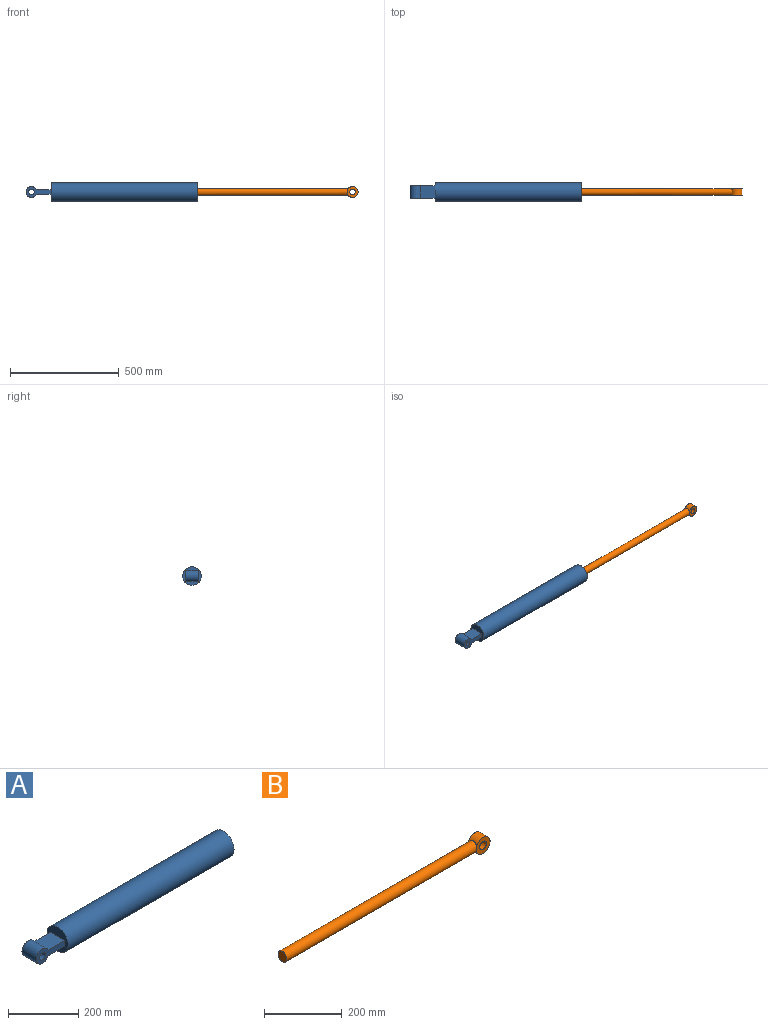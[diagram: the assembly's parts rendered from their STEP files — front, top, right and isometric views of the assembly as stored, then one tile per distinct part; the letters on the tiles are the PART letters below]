
ASSEMBLY  parts=2 mates=1
PART A: 11 faces, bbox 785x85x85 mm
  f0: cylinder r=42.5mm len=670mm, axis (-1,0,0), area 178913.7mm2, adj f1,f2
  f1: plane 85x85mm, normal (1,0,0), area 4870.3mm2, adj f0,f9
  f2: plane 85x85mm, normal (-1,0,0), area 4514.5mm2, adj f0,f3,f4,f5,f6
  f3: plane 67.09x58mm, normal (0,0,1), area 3891.1mm2, adj f2,f4,f6,f7
  f4: plane 115x50mm, normal (0,1,0), area 2786.3mm2, adj f2,f3,f5,f7,f8
  f5: plane 67.09x58mm, normal (0,0,-1), area 3891.1mm2, adj f2,f4,f6,f7
  f6: plane 115x50mm, normal (0,-1,0), area 2786.3mm2, adj f2,f3,f5,f7,f8
  f7: cylinder r=25mm len=58mm, axis (0,-1,0), area 7917.2mm2, adj f3,f4,f5,f6
  f8: cylinder r=12.5mm len=58mm, axis (0,-1,0), area 4555.3mm2, adj f4,f6
  f9: cylinder r=16mm len=650mm, axis (1,0,0), area 65345.1mm2, adj f1,f10
  f10: plane 32x32mm, normal (1,0,0), area 804.2mm2, adj f9
PART B: 8 faces, bbox 738x32x50 mm
  f0: cylinder r=25mm len=11.14mm, axis (0,-1,0), area 7.5mm2, adj f1,f5
  f1: cylinder r=16mm len=693.79mm, axis (-1,0,0), area 69446.8mm2, adj f0,f2,f3,f4
  f2: plane 32x32mm, normal (-1,0,0), area 804.2mm2, adj f1
  f3: cylinder r=25mm len=11.14mm, axis (0,-1,0), area 7.5mm2, adj f1,f6
  f4: cylinder r=25mm len=50mm, axis (0,1,0), area 3873.8mm2, adj f1,f5,f6
  f5: plane 50x50mm, normal (0,-1,0), area 1472.6mm2, adj f0,f4,f7
  f6: plane 50x50mm, normal (0,1,0), area 1472.6mm2, adj f3,f4,f7
  f7: cylinder r=12.5mm len=30mm, axis (0,-1,0), area 2356.2mm2, adj f5,f6
PLACE A t=(-334.72,38.62,-58.48)mm
PLACE B t=(-334.72,38.62,-58.48)mm
MATE slider A.f0 <-> B.f1  axis (-1,0,0) through (335.28,38.62,-58.48)mm
